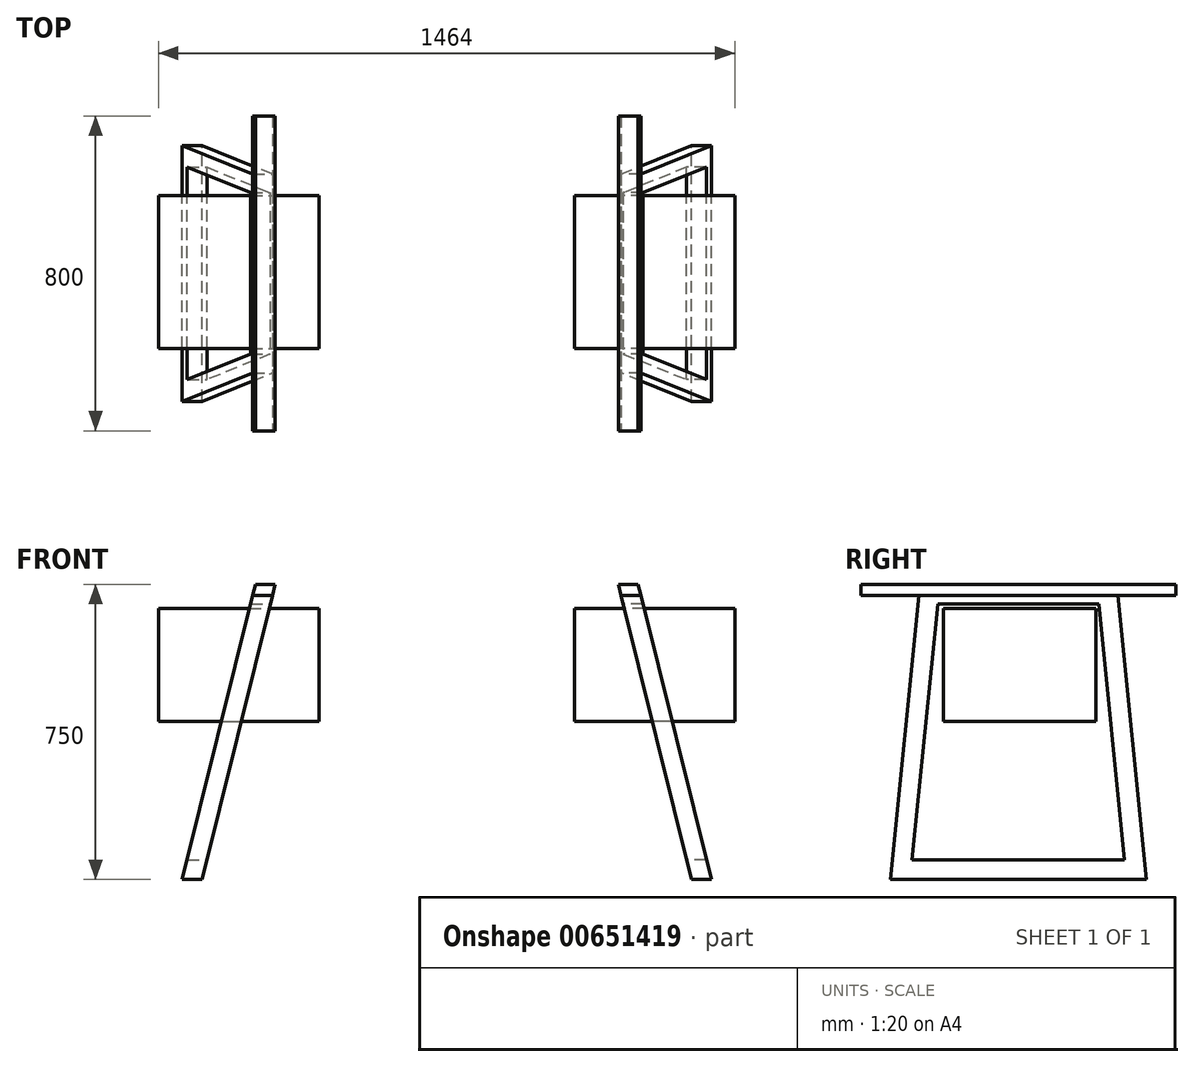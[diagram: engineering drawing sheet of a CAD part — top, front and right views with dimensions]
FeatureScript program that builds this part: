
annotation { "Feature Type Name" : "Feature", "Feature Type Description" : "" }
export const myFeature = defineFeature(function(context is Context, id is Id, definition is map)
    precondition{}
    {
        {
            assignVariable(context, id + "F0", {"name" : "w_desk", "anyValue" : 800});
        }
        {
            assignVariable(context, id + "F1", {"name" : "b_desk", "anyValue" : 1800});
        }
        {
            var Q0;
            Q0=qCreatedBy(makeId("Right.planeOp"),FACE);
            var sketch = newSketch(context, id + "F2", { "sketchPlane" : qUnion([Q0])});
            skLineSegment(sketch, "E0.bottom", {"start": v(-400, 750) * mm, "end": v(400, 750) * mm});
            skLineSegment(sketch, "E0.top", {"start": v(-400, 722) * mm, "end": v(400, 722) * mm});
            skLineSegment(sketch, "E0.left", {"start": v(-400, 750) * mm, "end": v(-400, 722) * mm});
            skLineSegment(sketch, "E0.right", {"start": v(400, 750) * mm, "end": v(400, 722) * mm});
            skLineSegment(sketch, "E1", {"start": v(0, 750) * mm, "end": v(0, 0) * mm, "construction": true});
            skLineSegment(sketch, "E2.bottom", {"start": v(-250, 750) * mm, "end": v(250, 750) * mm});
            skLineSegment(sketch, "E3", {"start": v(-250, 750) * mm, "end": v(-325, 0) * mm});
            skLineSegment(sketch, "E4", {"start": v(-325, 0) * mm, "end": v(325, 0) * mm});
            skLineSegment(sketch, "E5", {"start": v(325, 0) * mm, "end": v(250, 750) * mm});
            skLineSegment(sketch, "E6", {"start": v(-204.75, 700) * mm, "end": v(204.75, 700) * mm});
            skLineSegment(sketch, "E7", {"start": v(204.75, 700) * mm, "end": v(269.75, 50) * mm});
            skLineSegment(sketch, "E8", {"start": v(269.75, 50) * mm, "end": v(-269.75, 50) * mm});
            skLineSegment(sketch, "E9", {"start": v(-269.75, 50) * mm, "end": v(-204.75, 700) * mm});
            skLineSegment(sketch, "E10", {"start": v(0, 750) * mm, "end": v(0, 700) * mm, "construction": true});
            skLineSegment(sketch, "E11", {"start": v(0, 700) * mm, "end": v(0, 0) * mm, "construction": true});
            skLineSegment(sketch, "E12", {"start": v(0, 0) * mm, "end": v(0, 50) * mm, "construction": true});
            skLineSegment(sketch, "E13.top", {"start": v(-190.65, 401.74) * mm, "end": v(197.56, 401.74) * mm});
            skLineSegment(sketch, "E13.left", {"start": v(-190.65, 688.15) * mm, "end": v(-190.65, 401.74) * mm});
            skLineSegment(sketch, "E13.right", {"start": v(197.56, 688.15) * mm, "end": v(197.56, 401.74) * mm});
            skLineSegment(sketch, "E14", {"start": v(-190.65, 688.15) * mm, "end": v(197.56, 688.15) * mm});
            skSolve(sketch);
        }
        {
            var Q0;
            Q0=makeQuery(id+"F2.imprint","IMPRINT",FACE,{"disambiguationData":[TD([[makeQuery(id+"F2.imprint","IMPRINT",EDGE,{"derivedFrom":sQuery(id+"F2.wireOp",EDGE,"E0.bottom")}),-1.0]])]});
            var Q1;
            {var subQ0=sQuery(id+"F2.wireOp",EDGE,"E2.bottom");Q1=makeQuery(id+"F2.imprint","IMPRINT",FACE,{"disambiguationData":[TD([[makeQuery(id+"F2.imprint","IMPRINT",EDGE,{"derivedFrom":subQ0}),-1.0]])]});}
            var Q2;
            {var subQ6=sQuery(id+"F2.wireOp",EDGE,"E0.top");Q2=makeQuery(id+"F2.imprint","IMPRINT",FACE,{"disambiguationData":[TD([[makeQuery(id+"F2.imprint","IMPRINT",EDGE,{"derivedFrom":subQ6}),1.0]])]});}
            extrude(context, id + "F3", {"entities" : qUnion([Q0, Q1, Q2]), "depth" : (getVariable(context, 'b_desk') / 2) * mm, "offsetDistance" : 25 * mm});
        }
        {
            var Q0;
            Q0=makeQuery(id+"F2.imprint","IMPRINT",FACE,{"disambiguationData":[TD([[makeQuery(id+"F2.imprint","IMPRINT",EDGE,{"derivedFrom":sQuery(id+"F2.wireOp",EDGE,"E2.bottom")}),-1.0]])]});
            var Q1;
            {var subQ1=sQuery(id+"F2.wireOp",EDGE,"E6");Q1=makeQuery(id+"F2.imprint","IMPRINT",FACE,{"disambiguationData":[TD([[makeQuery(id+"F2.imprint","IMPRINT",EDGE,{"derivedFrom":subQ1}),1.0]])]});}
            var Q2;
            {var subQ6=sQuery(id+"F2.wireOp",EDGE,"E4");Q2=makeQuery(id+"F2.imprint","IMPRINT",FACE,{"disambiguationData":[TD([[makeQuery(id+"F2.imprint","IMPRINT",EDGE,{"derivedFrom":subQ6}),1.0]])]});}
            extrude(context, id + "F4", {"entities" : qUnion([Q0, Q1, Q2]), "depth" : (getVariable(context, 'b_desk') / 2) * mm, "offsetDistance" : 25 * mm, "hasSecondDirection" : true, "secondDirectionOppositeDirection" : false, "secondDirectionDepth" : 0 * mm});
        }
        {
            var Q0;
            Q0=qCreatedBy(makeId("Front.planeOp"),FACE);
            var sketch = newSketch(context, id + "F5", { "sketchPlane" : qUnion([Q0])});
            skLineSegment(sketch, "E15", {"start": v(671.92, 0) * mm, "end": v(485.93, 750) * mm});
            skLineSegment(sketch, "E16", {"start": v(671.92, 0) * mm, "end": v(621.92, 0) * mm});
            skLineSegment(sketch, "E17", {"start": v(621.92, 0) * mm, "end": v(435.93, 750) * mm});
            skLineSegment(sketch, "E18", {"start": v(435.93, 750) * mm, "end": v(485.93, 750) * mm});
            skSolve(sketch);
        }
        {
            var Q0;
            Q0=makeQuery(id+"F5.imprint","IMPRINT",FACE,{"disambiguationData":[TD([[makeQuery(id+"F5.imprint","IMPRINT",EDGE,{"derivedFrom":sQuery(id+"F5.wireOp",EDGE,"E15")}),1.0]])]});
            extrude(context, id + "F6", {"entities" : qUnion([Q0]), "operationType" : NewBodyOperationType.INTERSECT, "endBound" : BoundingType.SYMMETRIC, "depth" : (getVariable(context, 'w_desk')) * mm, "offsetDistance" : 25 * mm});
        }
        {
            var Q0;
            Q0=makeQuery(id+"F4.opExtrude","SWEPT_BODY",BODY,{"disambiguationData":[OSD([sQuery(id+"F2.wireOp",EDGE,"E2.bottom"),sQuery(id+"F2.wireOp",EDGE,"E3"),sQuery(id+"F2.wireOp",EDGE,"E4"),sQuery(id+"F2.wireOp",EDGE,"E5"),sQuery(id+"F2.wireOp",EDGE,"E6"),sQuery(id+"F2.wireOp",EDGE,"E7"),sQuery(id+"F2.wireOp",EDGE,"E8"),sQuery(id+"F2.wireOp",EDGE,"E9")])]});
            var Q1;
            Q1=makeQuery(id+"F3.opExtrude","SWEPT_BODY",BODY,{"disambiguationData":[OSD([sQuery(id+"F2.wireOp",EDGE,"E0.bottom"),sQuery(id+"F2.wireOp",EDGE,"E0.top"),sQuery(id+"F2.wireOp",EDGE,"E0.left"),sQuery(id+"F2.wireOp",EDGE,"E0.right"),sQuery(id+"F2.wireOp",EDGE,"E2.bottom")])]});
            booleanBodies(context, id + "F7", {"operationType" : BooleanOperationType.SUBTRACTION, "tools" : qUnion([Q0]), "targets" : qUnion([Q1]), "keepTools" : true});
        }
        {
            var Q0;
            Q0=makeQuery(id+"F3.opExtrude","SWEPT_BODY",BODY,{"disambiguationData":[OSD([sQuery(id+"F2.wireOp",EDGE,"E0.bottom"),sQuery(id+"F2.wireOp",EDGE,"E0.top"),sQuery(id+"F2.wireOp",EDGE,"E0.left"),sQuery(id+"F2.wireOp",EDGE,"E0.right"),sQuery(id+"F2.wireOp",EDGE,"E2.bottom")])]});
            var Q1;
            Q1=makeQuery(id+"F4.opExtrude","SWEPT_BODY",BODY,{"disambiguationData":[OSD([sQuery(id+"F2.wireOp",EDGE,"E2.bottom"),sQuery(id+"F2.wireOp",EDGE,"E3"),sQuery(id+"F2.wireOp",EDGE,"E4"),sQuery(id+"F2.wireOp",EDGE,"E5"),sQuery(id+"F2.wireOp",EDGE,"E6"),sQuery(id+"F2.wireOp",EDGE,"E7"),sQuery(id+"F2.wireOp",EDGE,"E8"),sQuery(id+"F2.wireOp",EDGE,"E9")])]});
            var Q2;
            Q2=qCreatedBy(makeId("Right.planeOp"),FACE);
            mirror(context, id + "F8", {"entities" : qUnion([Q0, Q1]), "mirrorPlane" : qUnion([Q2])});
        }
        {
            var Q0;
            Q0=makeQuery(id+"F2.imprint","IMPRINT",FACE,{"disambiguationData":[TD([[makeQuery(id+"F2.imprint","IMPRINT",EDGE,{"derivedFrom":sQuery(id+"F2.wireOp",EDGE,"E13.bottom")}),-1.0]])]});
            var Q1;
            {var subQ1=sQuery(id+"F2.wireOp",EDGE,"E13.top");Q1=makeQuery(id+"F2.imprint","IMPRINT",FACE,{"disambiguationData":[TD([[makeQuery(id+"F2.imprint","IMPRINT",EDGE,{"derivedFrom":subQ1}),1.0]])]});}
            extrude(context, id + "F9", {"entities" : qUnion([Q0, Q1]), "depth" : 732 * mm, "offsetDistance" : 25 * mm, "hasSecondDirection" : true, "secondDirectionOppositeDirection" : false, "secondDirectionDepth" : (650 / 2) * mm});
        }
        {
            var Q0;
            Q0=makeQuery(id+"F9.opExtrude","SWEPT_BODY",BODY,{"disambiguationData":[OSD([sQuery(id+"F2.wireOp",EDGE,"E13.bottom"),sQuery(id+"F2.wireOp",EDGE,"E13.top"),sQuery(id+"F2.wireOp",EDGE,"E13.left"),sQuery(id+"F2.wireOp",EDGE,"E13.right")])]});
            var Q1;
            Q1=qCreatedBy(makeId("Right.planeOp"),FACE);
            mirror(context, id + "F10", {"entities" : qUnion([Q0]), "mirrorPlane" : qUnion([Q1])});
        }
    });
